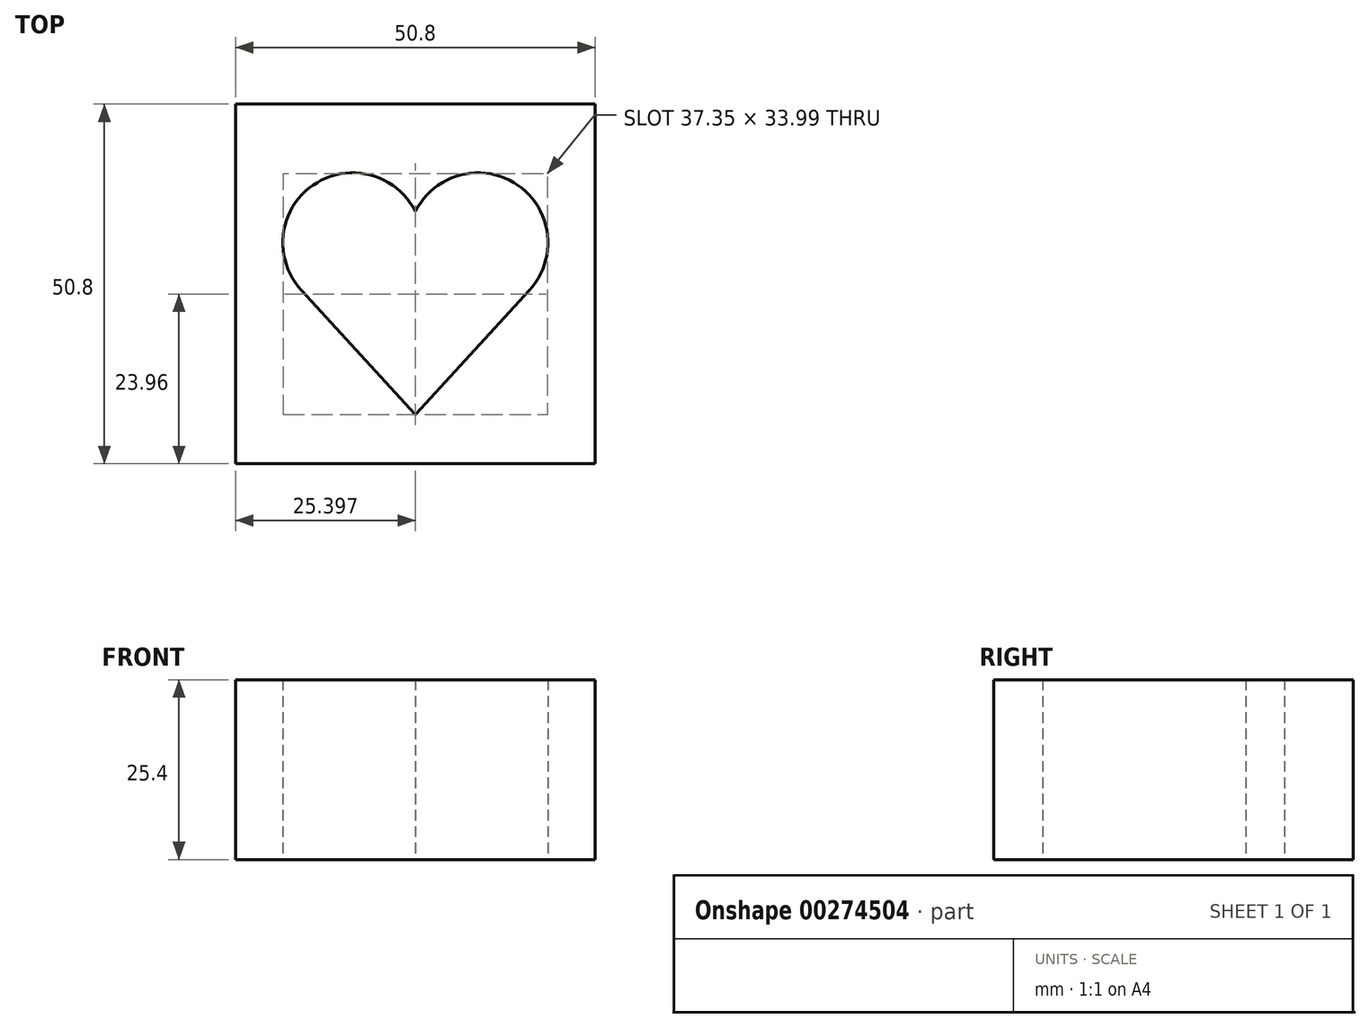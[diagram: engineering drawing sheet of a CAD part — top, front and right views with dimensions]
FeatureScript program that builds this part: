
annotation { "Feature Type Name" : "Feature", "Feature Type Description" : "" }
export const myFeature = defineFeature(function(context is Context, id is Id, definition is map)
    precondition{}
    {
        {
            var Q0;
            Q0=qCreatedBy(makeId("Top.planeOp"),FACE);
            var sketch = newSketch(context, id + "F0", { "sketchPlane" : qUnion([Q0])});
            skLineSegment(sketch, "E0.bottom", {"start": v(-39.1, 32.16) * mm, "end": v(11.7, 32.16) * mm});
            skLineSegment(sketch, "E0.top", {"start": v(-39.1, -18.64) * mm, "end": v(11.7, -18.64) * mm});
            skLineSegment(sketch, "E0.left", {"start": v(-39.1, 32.16) * mm, "end": v(-39.1, -18.64) * mm});
            skLineSegment(sketch, "E0.right", {"start": v(11.7, 32.16) * mm, "end": v(11.7, -18.64) * mm});
            skLineSegment(sketch, "E1", {"start": v(-13.7, 32.16) * mm, "end": v(-13.7, -18.64) * mm, "construction": true});
            skLineSegment(sketch, "E2", {"start": v(-39.1, 6.76) * mm, "end": v(11.7, 6.76) * mm, "construction": true});
            skCircle(sketch, "E3", {"center": v(-22.54, 12.58) * mm, "radius": 9.9 * mm});
            skLineSegment(sketch, "E4", {"start": v(-13.7, -11.67) * mm, "end": v(-30.63, 6.76) * mm});
            skCircle(sketch, "E5.MirrorC", {"center": v(-4.85, 12.58) * mm, "radius": 9.9 * mm});
            skLineSegment(sketch, "E6.MirrorCS", {"start": v(-13.7, -11.67) * mm, "end": v(3.24, 6.76) * mm});
            skSolve(sketch);
        }
        {
            var Q0;
            Q0=makeQuery(id+"F0.imprint","IMPRINT",FACE,{"disambiguationData":[TD([[makeQuery(id+"F0.imprint","IMPRINT",EDGE,{"derivedFrom":sQuery(id+"F0.wireOp",EDGE,"E0.bottom")}),-1.0]])]});
            extrude(context, id + "F1", {"entities" : qUnion([Q0]), "depth" : 25.4 * mm});
        }
    });
